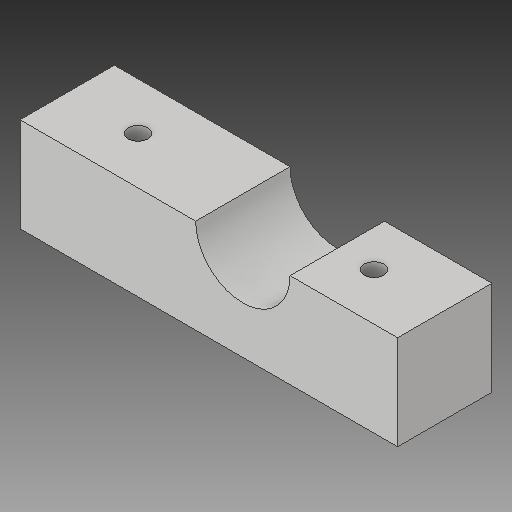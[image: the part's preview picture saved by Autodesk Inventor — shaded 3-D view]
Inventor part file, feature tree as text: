
AUTODESK INVENTOR PART (.ipt)
format: ipt  version: 2019.3 (Build 233278000, 278)  size: 131,072 bytes
history: native  units: in
note: dims shown in document units (in); Inventor stores cm internally (conversion verified against a paired STEP export)
features: other x5, sketch x4, extrude x3, hole x1, projected_geometry x1, reference x1
ambient origin geometry x8: Origin, YZ Plane, XZ Plane, XY Plane, X Axis, Y Axis, Z Axis, Center Point
bodies: Solid1 (feature_tree)
feature tree (15):
  extrude  "Extrusion1"  Depth=0.5in
  extrude  "Extrusion2"  Depth=0.5in TaperAngle=0.0deg
  hole  "Hole1"  [1 undecoded]
  extrude  "Extrusion4"  Depth=0.281in
  sketch  "Sketch1"  dims[d0=2.0in d1=0.5in]
  sketch  "Sketch3"  dims[d2=0.5in d3=0.0in d4=1.0in d5=0.0in]
  projected_geometry  "Projected Loop1"
  reference  "Reference1"
  sketch  "Sketch4"  dims[d6=0.375in d7=0.375in]
  sketch  "Sketch7"  dims[d8=0.104in d9=0.276in d10=0.375in d11=0.25in d12=0.5635in d13=0.432in d14=0.8108in d18=0.191in d19=0.281in d20=0.0in]
  parser-record x1  (decoder bookkeeping rows leaked as tree rows — omitted from the tree; the rows remain in map.json)
  other  "FocuserAssembly.iam"
  other  "WormDrive02:1"
  other  "Worm Gears:1"
  other  "Worm:1"
note: 1 required parameter value undecoded (feature->parameter linkage not recoverable at this tier; creation-order binding heuristic only, values carry confidence <= 0.55)
note: 1 file-system path scrubbed to <path> (originals preserved in map.json)
